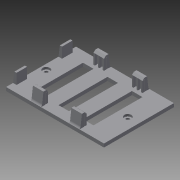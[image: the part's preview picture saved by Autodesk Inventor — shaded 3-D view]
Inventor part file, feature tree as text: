
AUTODESK INVENTOR PART (.ipt)
format: ipt  version: 2014 SP1 (Build 180222100, 222)  size: 322,048 bytes
history: native  units: in
note: dims shown in document units (in); Inventor stores cm internally (conversion verified against a paired STEP export)
features: extrude x11, sketch x11, fillet x1
ambient origin geometry x8: Origin, YZ Plane, XZ Plane, XY Plane, X Axis, Y Axis, Z Axis, Center Point
bodies: Solid1 (feature_tree)
feature tree (23):
  extrude  "Extrusion1"  Depth=2.5in
  extrude  "Extrusion2"  Depth=0.375in TaperAngle=0.0deg
  extrude  "Extrusion3"  Depth=0.438in TaperAngle=0.0deg
  extrude  "Extrusion4"  Depth=0.125in
  extrude  "Extrusion5"  Depth=0.125in
  fillet  "Fillet1"  Radius=0.063in
  extrude  "Extrusion6"  Depth=1.75in
  extrude  "Extrusion7"  Depth=0.125in TaperAngle=0.0deg
  extrude  "Extrusion8"  Depth=0.372in TaperAngle=0.0deg
  extrude  "Extrusion9"  Depth=0.08in
  extrude  "Extrusion10"  [1 undecoded]
  extrude  "Extrusion11"  [1 undecoded]
  sketch  "Sketch1"  dims[d0=3.5in d1=2.5in]
  sketch  "Sketch2"  dims[d2=0.125in d3=0.0in d4=0.375in d5=0.0in]
  sketch  "Sketch3"  dims[d7=2.0in d8=0.0in d15=0.438in d16=0.0in]
  sketch  "Sketch4"  dims[d17=0.07in d18=0.125in]
  sketch  "Sketch5"  dims[d19=1.75in d20=0.0in d21=0.125in d23=0.063in d24=0.0in]
  sketch  "Sketch6"  dims[d26=1.75in d27=0.0in d29=2.914in]
  sketch  "Sketch7"  dims[d30=0.075in d31=0.0in d32=0.125in d33=0.0in]
  sketch  "Sketch8"  dims[d34=0.08in d35=0.372in d36=0.0in]
  sketch  "Sketch9"  dims[d37=1.75in d38=0.0in d40=0.08in]
  sketch  "Sketch10"
  sketch  "Sketch11"
note: 2 required parameter values undecoded (feature->parameter linkage not recoverable at this tier; creation-order binding heuristic only, values carry confidence <= 0.55)
